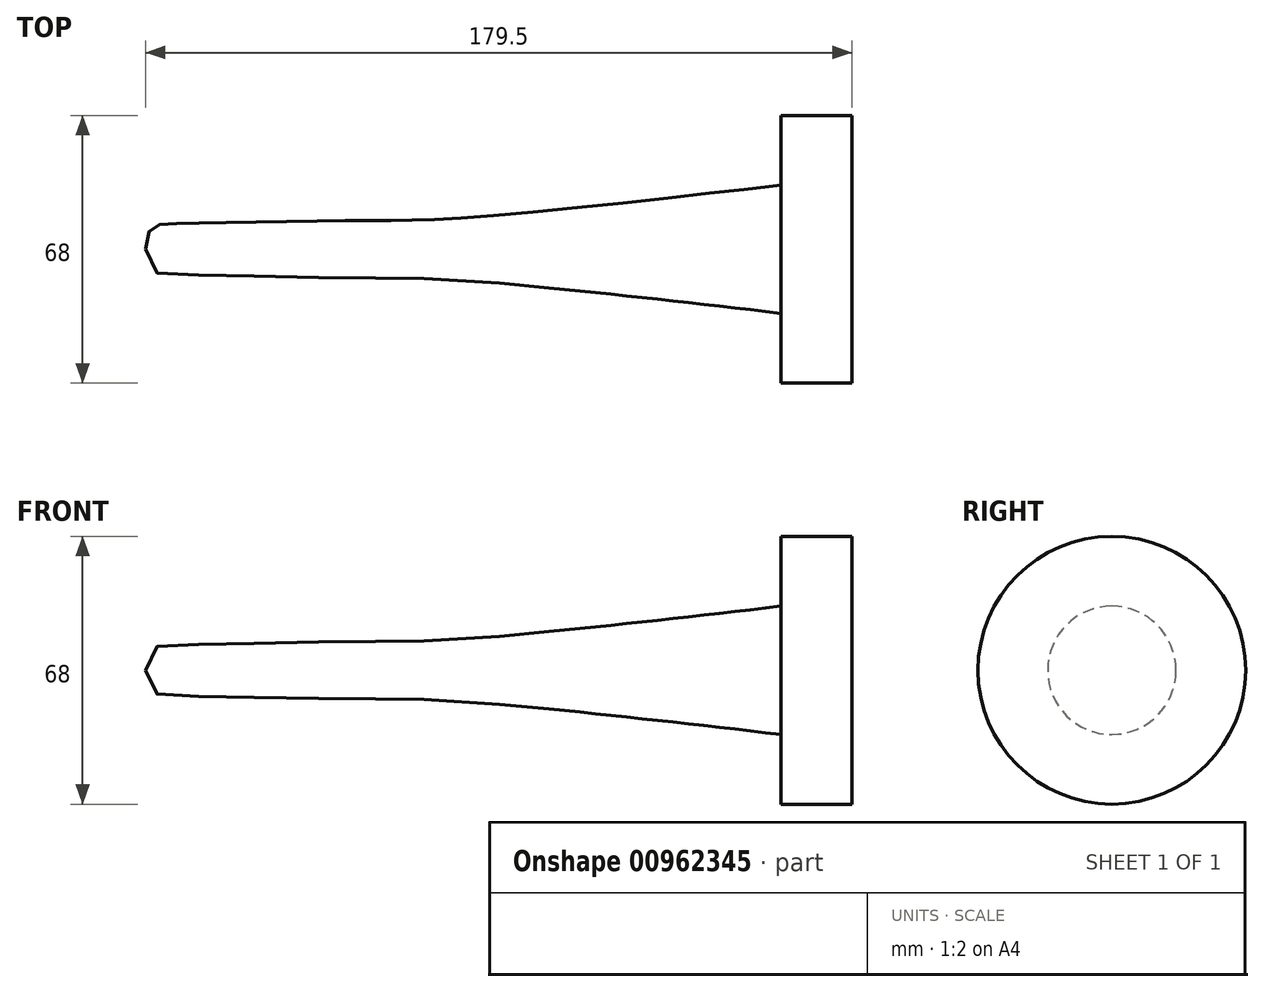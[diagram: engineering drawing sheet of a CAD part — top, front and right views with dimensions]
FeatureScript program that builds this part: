
annotation { "Feature Type Name" : "Feature", "Feature Type Description" : "" }
export const myFeature = defineFeature(function(context is Context, id is Id, definition is map)
    precondition{}
    {
        {
            var Q0;
            Q0=qCreatedBy(makeId("Top.planeOp"),FACE);
            var sketch = newSketch(context, id + "F0", { "sketchPlane" : qUnion([Q0])});
            skLineSegment(sketch, "E0", {"start": v(0, 0) * mm, "end": v(179.5, 0) * mm});
            skLineSegment(sketch, "E1", {"start": v(179.5, 0) * mm, "end": v(179.5, 34) * mm});
            skLineSegment(sketch, "E2", {"start": v(179.5, 34) * mm, "end": v(161.5, 34) * mm});
            skLineSegment(sketch, "E3", {"start": v(161.5, 34) * mm, "end": v(161.5, 16.3) * mm});
            skFitSpline(sketch, "E4", {"points": [v(0, 0) * mm, v(8, 6.5) * mm, v(53, 7.3) * mm, v(86.9, 8.4) * mm, v(161.5, 16.3) * mm], "startDerivative": vector(0, 148.22) * mm, "endDerivative": vector(30.84, 3.6) * mm});
            skSolve(sketch);
        }
        {
            var Q0;
            Q0=makeQuery(id+"F0.imprint","IMPRINT",FACE,{"disambiguationData":[TD([[makeQuery(id+"F0.imprint","IMPRINT",EDGE,{"derivedFrom":sQuery(id+"F0.wireOp",EDGE,"E0")}),1.0]])]});
            var Q1;
            Q1=sQuery(id+"F0.wireOp",EDGE,"E0");
            revolve(context, id + "F1", {"surfaceOperationType" : NewSurfaceOperationType.NEW, "entities" : qUnion([Q0]), "axis" : qUnion([Q1]), "revolveType" : RevolveType.FULL});
        }
    });
